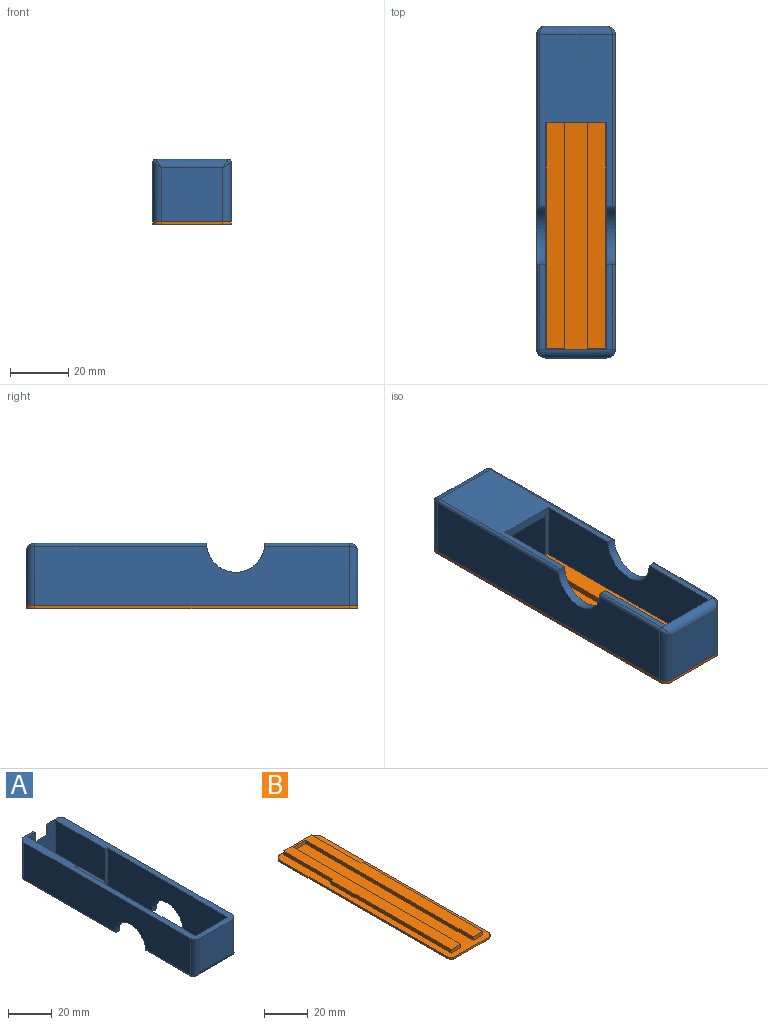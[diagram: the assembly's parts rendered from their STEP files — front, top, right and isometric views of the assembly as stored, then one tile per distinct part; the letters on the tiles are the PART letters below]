
ASSEMBLY  parts=2 mates=1
PART A: 48 faces, bbox 27x114x21.5 mm
  f0: plane 32.1x18.5mm, normal (0,0,1), area 548.8mm2, adj f10,f11,f12,f13,f35,f36,f37,f38
  f1: plane 114x27mm, normal (0,0,1), area 831.2mm2, adj f4,f5,f6,f7,f8,f9,f10,f11
  f2: plane 29x2mm, normal (0,0,-1), area 58mm2, adj f7,f17,f19,f28
  f3: plane 59x25mm, normal (0,0,-1), area 866mm2, adj f7,f9,f10,f16,f17,f22,f24,f26
  f4: plane 108x20.5mm, normal (-1,0,0), area 2076.9mm2, adj f1,f16,f20,f21,f26,f30
  f5: plane 21x18.5mm, normal (0,-1,0), area 388.5mm2, adj f1,f18,f19,f20
  f6: plane 108x20.5mm, normal (1,0,0), area 2076.9mm2, adj f1,f17,f18,f23,f24,f28
  f7: plane 78x21.5mm, normal (-1,0,0), area 1519.9mm2, adj f1,f2,f3,f8,f10,f17
  f8: plane 21.5x21mm, normal (0,1,0), area 451.5mm2, adj f1,f7,f9,f19
  f9: plane 78x21.5mm, normal (1,0,0), area 1519.9mm2, adj f1,f3,f8,f10,f15,f16
  f10: plane 21.5x21mm, normal (0,-1,0), area 109.3mm2, adj f0,f1,f3,f7,f9,f11,f13
  f11: plane 32.1x18.5mm, normal (1,0,0), area 593.8mm2, adj f0,f1,f10,f12
  f12: plane 18.5x18.5mm, normal (0,-1,0), area 294.2mm2, adj f0,f1,f11,f13,f32,f33,f34
  f13: plane 32.1x18.5mm, normal (-1,0,0), area 593.8mm2, adj f0,f1,f10,f12
  f14: plane 21x18.5mm, normal (0,1,0), area 340.5mm2, adj f1,f21,f22,f23,f32,f33,f34
  f15: plane 29x2mm, normal (0,0,-1), area 58mm2, adj f9,f16,f19,f30
  f16: cylinder r=10mm len=20mm, axis (1,0,0), area 93.8mm2, adj f3,f4,f9,f15,f26,f30
  f17: cylinder r=10mm len=20mm, axis (1,0,0), area 93.8mm2, adj f2,f3,f6,f7,f24,f28
  f18: cylinder r=3mm len=20.5mm, axis (0,0,1), area 93.2mm2, adj f1,f5,f6,f29
  f19: cylinder r=3mm len=25mm, axis (1,0,0), area 111mm2, adj f2,f5,f8,f15,f29,f31
  f20: cylinder r=3mm len=20.5mm, axis (0,0,-1), area 93.2mm2, adj f1,f4,f5,f31
  f21: cylinder r=3mm len=20.5mm, axis (0,0,1), area 93.2mm2, adj f1,f4,f14,f27
  f22: cylinder r=3mm len=25mm, axis (-1,0,0), area 111mm2, adj f3,f14,f25,f27
  f23: cylinder r=3mm len=20.5mm, axis (0,0,-1), area 93.2mm2, adj f1,f6,f14,f25
  f24: cylinder r=1mm len=59.05mm, axis (0,1,0), area 92.7mm2, adj f3,f6,f17,f25
  f25: bspline ~3.52x3mm, area 5mm2, adj f22,f23,f24
  f26: cylinder r=1mm len=59.05mm, axis (0,-1,0), area 92.7mm2, adj f3,f4,f16,f27
  f27: bspline ~3.52x3mm, area 5mm2, adj f21,f22,f26
  f28: cylinder r=1mm len=29.05mm, axis (0,1,0), area 45.6mm2, adj f2,f6,f17,f29
  f29: bspline ~3.52x3mm, area 5mm2, adj f18,f19,f28
  f30: cylinder r=1mm len=29.05mm, axis (0,-1,0), area 45.6mm2, adj f4,f15,f16,f31
  f31: bspline ~3.52x3mm, area 5mm2, adj f19,f20,f30
  f32: plane 6x0.9mm, normal (-1,0,0), area 5.4mm2, adj f1,f12,f14,f33
  f33: plane 8x0.9mm, normal (0,0,1), area 7.2mm2, adj f12,f14,f32,f34
  f34: plane 6x0.9mm, normal (1,0,0), area 5.4mm2, adj f1,f12,f14,f33
  f35: plane 3x1mm, normal (1,0,0), area 3mm2, adj f0,f36,f46,f47
  f36: plane 3x1mm, normal (0,1,0), area 3mm2, adj f0,f35,f37,f47
  f37: plane 3x1mm, normal (1,0,0), area 3mm2, adj f0,f36,f38,f47
  f38: plane 3x1mm, normal (0,1,0), area 3mm2, adj f0,f37,f39,f47
  f39: plane 3x1mm, normal (-1,0,0), area 3mm2, adj f0,f38,f40,f47
  f40: plane 3x1mm, normal (0,1,0), area 3mm2, adj f0,f39,f41,f47
  f41: plane 3x1mm, normal (-1,0,0), area 3mm2, adj f0,f40,f42,f47
  f42: plane 3x1mm, normal (0,-1,0), area 3mm2, adj f0,f41,f43,f47
  f43: plane 3x1mm, normal (-1,0,0), area 3mm2, adj f0,f42,f44,f47
  f44: plane 3x1mm, normal (0,-1,0), area 3mm2, adj f0,f43,f45,f47
  f45: plane 3x1mm, normal (1,0,0), area 3mm2, adj f0,f44,f46,f47
  f46: plane 3x1mm, normal (0,-1,0), area 3mm2, adj f0,f35,f45,f47
  f47: plane 9x9mm, normal (0,0,1), area 45mm2, adj f35,f36,f37,f38,f39,f40,f41,f42
PART B: 23 faces, bbox 27x114x3 mm
  f0: plane 6.28x2mm, normal (0,-1,0), area 12.5mm2, adj f1,f6,f12,f21
  f1: plane 109.65x20.55mm, normal (0,0,1), area 1305.4mm2, adj f0,f8,f9,f10,f11,f12,f13,f14
  f2: plane 108x1mm, normal (-1,0,0), area 108mm2, adj f6,f7,f16,f19
  f3: plane 21x1mm, normal (0,-1,0), area 21mm2, adj f6,f7,f16,f17
  f4: plane 108x1mm, normal (1,0,0), area 108mm2, adj f6,f7,f17,f18
  f5: plane 21x1mm, normal (0,1,0), area 21mm2, adj f6,f7,f18,f19
  f6: plane 114x27mm, normal (0,0,1), area 1764.9mm2, adj f0,f2,f3,f4,f5,f8,f9,f10
  f7: plane 114x27mm, normal (0,0,-1), area 3070.3mm2, adj f2,f3,f4,f5,f16,f17,f18,f19
  f8: plane 31.8x2mm, normal (1,0,0), area 63.6mm2, adj f1,f6,f9,f15
  f9: plane 18.1x2mm, normal (0,1,0), area 36.2mm2, adj f1,f6,f8,f10
  f10: plane 31.8x2mm, normal (-1,0,0), area 63.6mm2, adj f1,f6,f9,f11
  f11: plane 2x1.23mm, normal (0,1,0), area 2.4mm2, adj f1,f6,f10,f12
  f12: plane 77.85x2mm, normal (-1,0,0), area 155.7mm2, adj f0,f1,f6,f11
  f13: plane 6.28x2mm, normal (0,-1,0), area 12.5mm2, adj f1,f6,f14,f22
  f14: plane 77.85x2mm, normal (1,0,0), area 155.7mm2, adj f1,f6,f13,f15
  f15: plane 2x1.23mm, normal (0,1,0), area 2.4mm2, adj f1,f6,f8,f14
  f16: cylinder r=3mm len=3mm, axis (0,0,-1), area 4.7mm2, adj f2,f3,f6,f7
  f17: cylinder r=3mm len=3mm, axis (0,0,1), area 4.7mm2, adj f3,f4,f6,f7
  f18: cylinder r=3mm len=3mm, axis (0,0,-1), area 4.7mm2, adj f4,f5,f6,f7
  f19: cylinder r=3mm len=3mm, axis (0,0,1), area 4.7mm2, adj f2,f5,f6,f7
  f20: plane 8x2mm, normal (0,-1,0), area 16mm2, adj f1,f6,f21,f22
  f21: plane 108.75x2mm, normal (1,0,0), area 217.5mm2, adj f0,f1,f6,f20
  f22: plane 108.75x2mm, normal (-1,0,0), area 217.5mm2, adj f1,f6,f13,f20
PLACE A rot(axis=(0,1,0),180deg) t=(-35.24,-15.83,27.78)mm
PLACE B t=(-35.24,-15.83,5.28)mm
MATE fastened A.f1 <-> B.f6  axis (0,0,-1) through (-35.24,-72.83,6.28)mm
